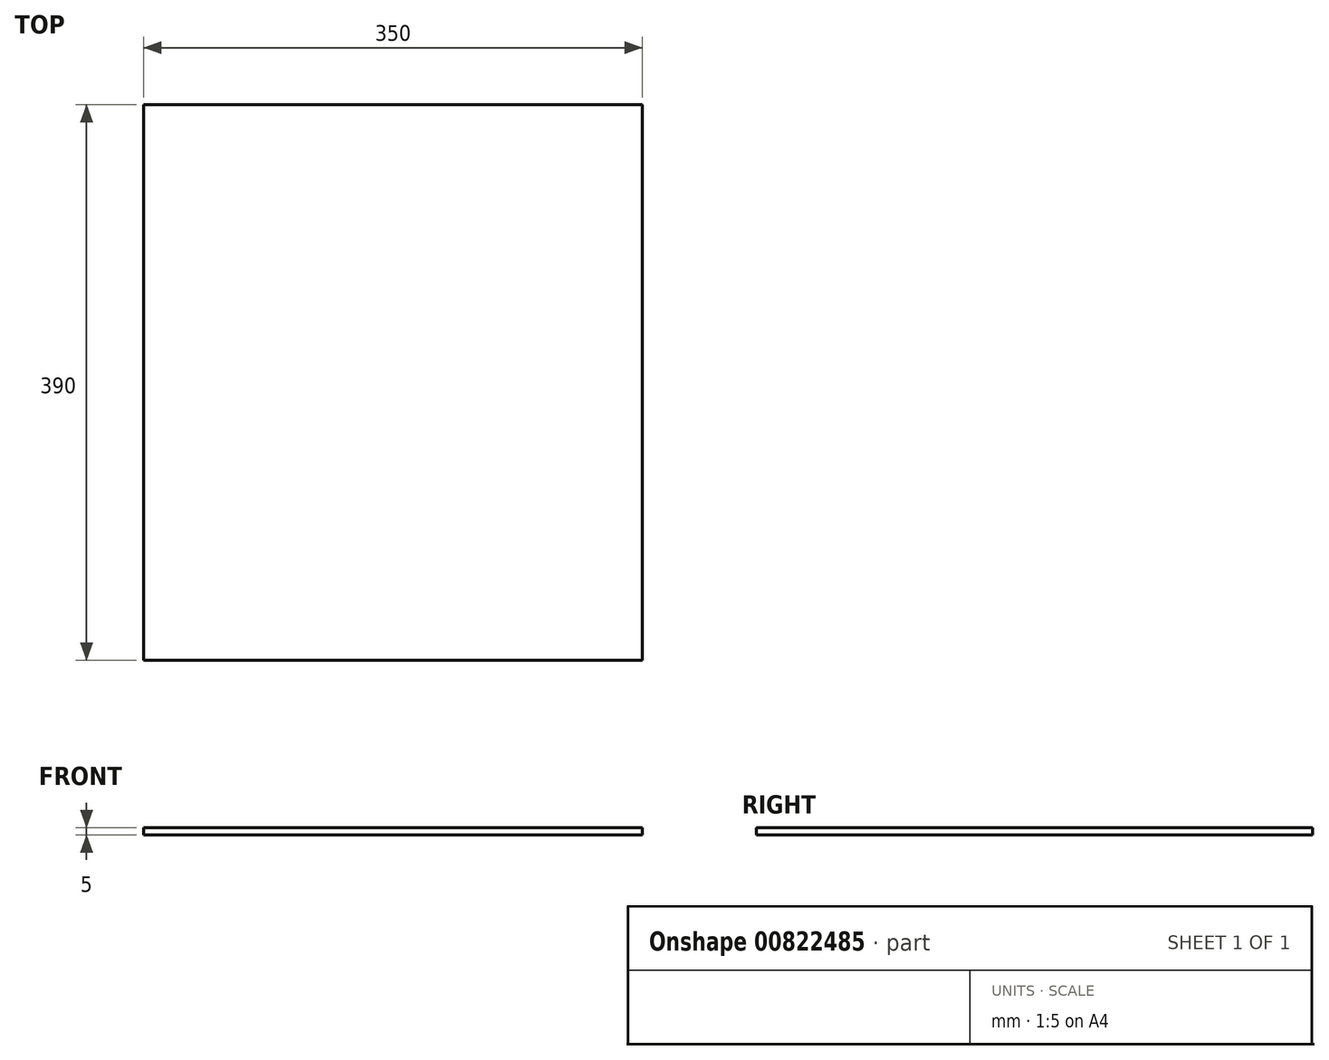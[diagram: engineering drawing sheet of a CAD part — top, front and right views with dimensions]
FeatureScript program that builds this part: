
annotation { "Feature Type Name" : "Feature", "Feature Type Description" : "" }
export const myFeature = defineFeature(function(context is Context, id is Id, definition is map)
    precondition{}
    {
        {
            var Q0;
            Q0=qCreatedBy(makeId("Top.planeOp"),FACE);
            var sketch = newSketch(context, id + "F0", { "sketchPlane" : qUnion([Q0])});
            skLineSegment(sketch, "E0.bottom", {"start": v(-224.64, 175.62) * mm, "end": v(125.36, 175.62) * mm});
            skLineSegment(sketch, "E0.top", {"start": v(-224.64, -214.38) * mm, "end": v(125.36, -214.38) * mm});
            skLineSegment(sketch, "E0.left", {"start": v(-224.64, 175.62) * mm, "end": v(-224.64, -214.38) * mm});
            skLineSegment(sketch, "E0.right", {"start": v(125.36, 175.62) * mm, "end": v(125.36, -214.38) * mm});
            skSolve(sketch);
        }
        {
            var Q0;
            Q0=makeQuery(id+"F0.imprint","IMPRINT",FACE,{"disambiguationData":[TD([[makeQuery(id+"F0.imprint","IMPRINT",EDGE,{"derivedFrom":sQuery(id+"F0.wireOp",EDGE,"E0.bottom")}),-1.0]])]});
            extrude(context, id + "F1", {"entities" : qUnion([Q0]), "depth" : 5 * mm, "offsetDistance" : 25.4 * mm});
        }
    });
